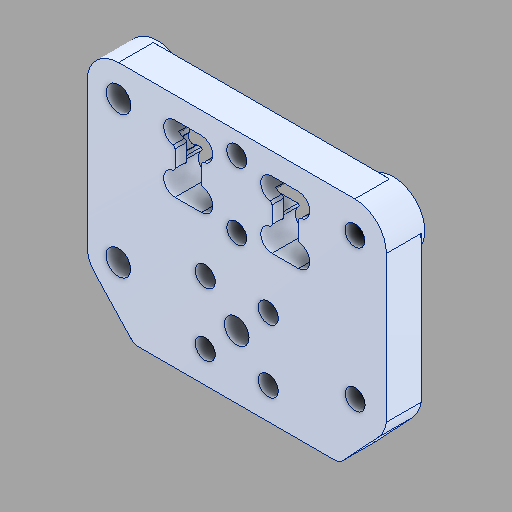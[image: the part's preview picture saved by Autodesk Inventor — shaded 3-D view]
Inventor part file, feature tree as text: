
AUTODESK INVENTOR PART (.ipt)
format: ipt  version: 2024.2 (Build 282272000, 272)  size: 246,784 bytes
history: native  units: in
note: dims shown in document units (in); Inventor stores cm internally (conversion verified against a paired STEP export)
features: fillet x1
ambient origin geometry x8: Origin, YZ Plane, XZ Plane, XY Plane, X Axis, Y Axis, Z Axis, Center Point
bodies: Solid1 (feature_tree)
feature tree (1):
  fillet  "Fillet9"  [1 undecoded]
note: 1 required parameter value undecoded (feature->parameter linkage not recoverable at this tier; creation-order binding heuristic only, values carry confidence <= 0.55)
